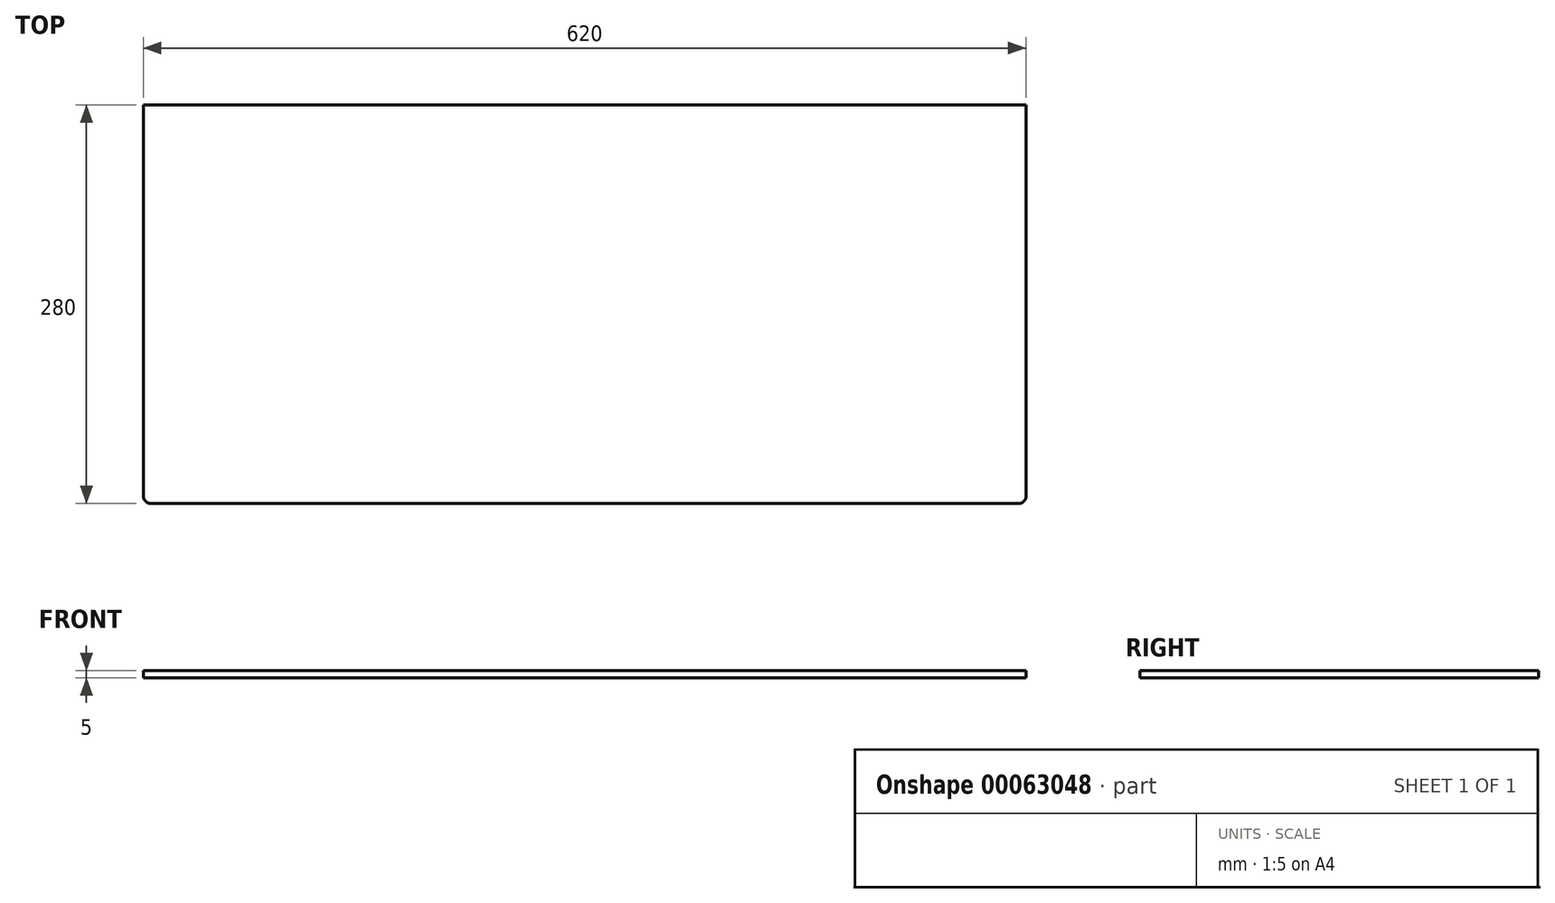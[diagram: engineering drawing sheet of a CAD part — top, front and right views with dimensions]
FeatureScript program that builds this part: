
annotation { "Feature Type Name" : "Feature", "Feature Type Description" : "" }
export const myFeature = defineFeature(function(context is Context, id is Id, definition is map)
    precondition{}
    {
        {
            var Q0;
            Q0=qCreatedBy(makeId("Top.planeOp"),FACE);
            var sketch = newSketch(context, id + "F0", { "sketchPlane" : qUnion([Q0])});
            skLineSegment(sketch, "E0", {"start": v(-5, 0) * mm, "end": v(-615, 0) * mm});
            skLineSegment(sketch, "E1", {"start": v(-620, 5) * mm, "end": v(-620, 280) * mm});
            skLineSegment(sketch, "E2", {"start": v(-620, 280) * mm, "end": v(0, 280) * mm});
            skLineSegment(sketch, "E3", {"start": v(0, 280) * mm, "end": v(0, 5) * mm});
            skPoint(sketch, "E4.visualSharp", {"position": v(-620, 0) * mm});
            skArc(sketch, "E4.filletArc", {"start": v(-620, 5) * mm, "mid": v(-618.54, 1.46) * mm, "end": v(-615, 0) * mm});
            skPoint(sketch, "E5.visualSharp", {"position": v(0, 0) * mm});
            skArc(sketch, "E5.filletArc", {"start": v(-5, 0) * mm, "mid": v(-1.46, 1.46) * mm, "end": v(0, 5) * mm});
            skSolve(sketch);
        }
        {
            var Q0;
            Q0=makeQuery(id+"F0.imprint","IMPRINT",FACE,{"disambiguationData":[TD([[makeQuery(id+"F0.imprint","IMPRINT",EDGE,{"derivedFrom":sQuery(id+"F0.wireOp",EDGE,"E0")}),-1.0]])]});
            extrude(context, id + "F1", {"entities" : qUnion([Q0]), "depth" : 5 * mm});
        }
    });
